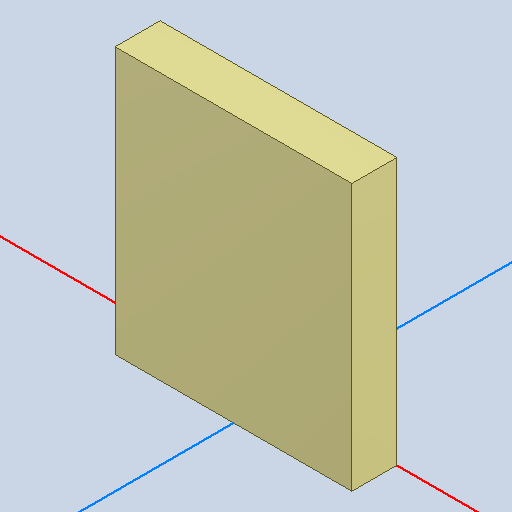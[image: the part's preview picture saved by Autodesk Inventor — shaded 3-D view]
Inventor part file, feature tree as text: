
AUTODESK INVENTOR PART (.ipt)
format: ipt  version: 2022 (Build 260153000, 153)  size: 91,136 bytes
history: native  units: mm
features: other x2, extrude x1
ambient origin geometry x8: Origin, YZ Plane, XZ Plane, XY Plane, X Axis, Y Axis, Z Axis, Center Point
bodies: Body1 (feature_tree)
feature tree (3):
  other  "Твердое тело1"
  extrude  "Выдавливание1"  Depth=1.0mm TaperAngle=0.0deg
  other  "LED5MM, LED5MM_8"
